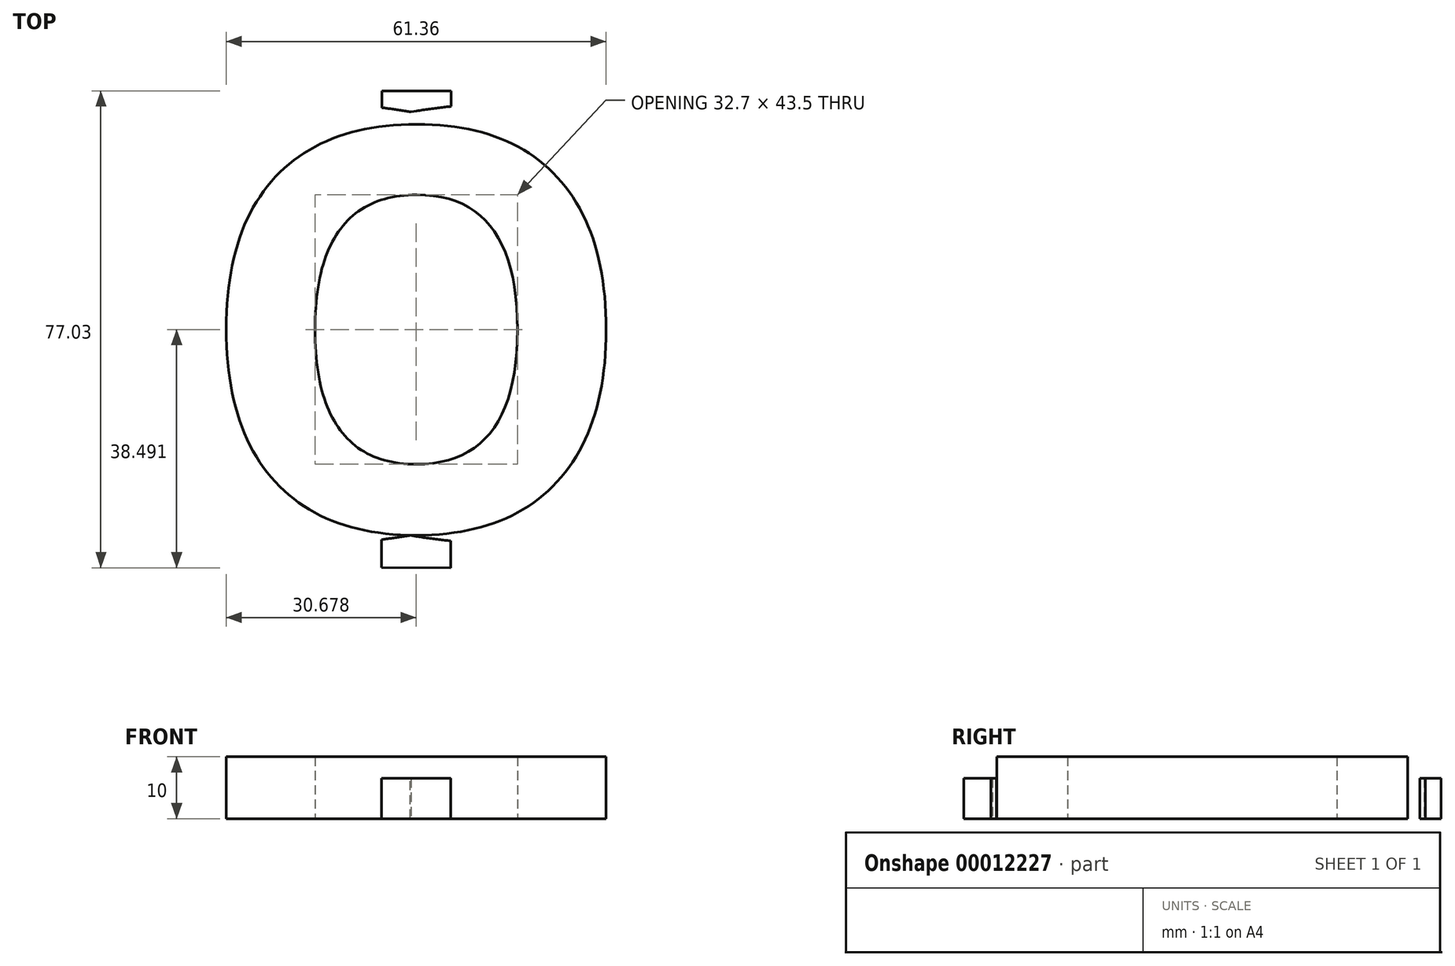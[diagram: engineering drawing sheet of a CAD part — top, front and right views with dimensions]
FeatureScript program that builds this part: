
annotation { "Feature Type Name" : "Feature", "Feature Type Description" : "" }
export const myFeature = defineFeature(function(context is Context, id is Id, definition is map)
    precondition{}
    {
        {
            var Q0;
            Q0=qCreatedBy(makeId("Top.planeOp"),FACE);
            var sketch = newSketch(context, id + "F0", { "sketchPlane" : qUnion([Q0])});
            skText(sketch, "E0", { "text": "O\n", "fontName": "OpenSans-Bold.ttf"});
            const initialGuessF0  = {"E0": [-0.0666, 0, 1, 0, 0.065]};
            skSetInitialGuess(sketch, initialGuessF0);
            skSolve(sketch);
        }
        {
            var Q0;
            Q0=makeQuery(id+"F0.imprint","IMPRINT",FACE,{"disambiguationData":[TD([[makeQuery(id+"F0.imprint","IMPRINT",EDGE,{"derivedFrom":sQuery(id+"F0.wireOp",EDGE,"E0.sketch_text.stroke-0")}),-1.0]])]});
            extrude(context, id + "F1", {"entities" : qUnion([Q0]), "depth" : 10 * mm});
        }
        {
            var Q0;
            Q0=qCreatedBy(makeId("Top.planeOp"),FACE);
            var sketch = newSketch(context, id + "F2", { "sketchPlane" : qUnion([Q0])});
            skFitSpline(sketch, "E1.0.0", {"points": [v(-8.18, 7.95) * mm, v(0, 16.8) * mm, v(0, 33.31) * mm]});
            skFitSpline(sketch, "E1.0.1", {"points": [v(0, 33.31) * mm, v(0, 49.84) * mm, v(-8.11, 58.66) * mm]});
            skFitSpline(sketch, "E1.0.2", {"points": [v(-8.11, 58.66) * mm, v(-16.23, 67.48) * mm, v(-31.54, 67.48) * mm]});
            skFitSpline(sketch, "E1.0.3", {"points": [v(-31.54, 67.48) * mm, v(-46.85, 67.48) * mm, v(-55.05, 58.73) * mm]});
            skFitSpline(sketch, "E1.0.4", {"points": [v(-55.05, 58.73) * mm, v(-63.25, 49.99) * mm, v(-63.25, 33.4) * mm]});
            skFitSpline(sketch, "E1.0.5", {"points": [v(-63.25, 33.4) * mm, v(-63.25, 16.8) * mm, v(-55.07, 7.95) * mm]});
            skFitSpline(sketch, "E1.0.6", {"points": [v(-55.07, 7.95) * mm, v(-46.9, -0.92) * mm, v(-31.62, -0.92) * mm]});
            skFitSpline(sketch, "E1.0.7", {"points": [v(-31.62, -0.92) * mm, v(-16.36, -0.92) * mm, v(-8.18, 7.95) * mm]});
            skLineSegment(sketch, "E2", {"start": v(-61.36, 32.4) * mm, "end": v(-61.36, 65.47) * mm, "construction": true});
            skLineSegment(sketch, "E3", {"start": v(-61.36, 65.47) * mm, "end": v(-30.6, 65.47) * mm, "construction": true});
            skLineSegment(sketch, "E4", {"start": v(-30.6, 65.47) * mm, "end": v(0, 65.47) * mm, "construction": true});
            skLineSegment(sketch, "E5", {"start": v(0, 65.47) * mm, "end": v(0, 32.32) * mm, "construction": true});
            skLineSegment(sketch, "E6", {"start": v(0, 0) * mm, "end": v(0, -0.89) * mm, "construction": true});
            skLineSegment(sketch, "E7", {"start": v(0, -0.89) * mm, "end": v(-30.68, -0.89) * mm, "construction": true});
            skLineSegment(sketch, "E8", {"start": v(-30.68, -0.89) * mm, "end": v(-61.36, -0.89) * mm, "construction": true});
            skLineSegment(sketch, "E9", {"start": v(-61.36, -0.89) * mm, "end": v(-61.36, 32.4) * mm, "construction": true});
            skLineSegment(sketch, "E10", {"start": v(-61.36, 0) * mm, "end": v(0, 0) * mm, "construction": true});
            skLineSegment(sketch, "E11", {"start": v(-61.36, 64.47) * mm, "end": v(0, 64.47) * mm, "construction": true});
            skLineSegment(sketch, "E12.bottom", {"start": v(-30.6, 64.47) * mm, "end": v(-36.2, 64.47) * mm});
            skLineSegment(sketch, "E12.top", {"start": v(-30.6, 70.87) * mm, "end": v(-36.2, 70.87) * mm});
            skLineSegment(sketch, "E12.left", {"start": v(-30.6, 64.47) * mm, "end": v(-30.6, 70.87) * mm});
            skLineSegment(sketch, "E12.right", {"start": v(-36.2, 64.47) * mm, "end": v(-36.2, 70.87) * mm});
            skLineSegment(sketch, "E13.bottom", {"start": v(-30.6, 64.47) * mm, "end": v(-25, 64.47) * mm});
            skLineSegment(sketch, "E13.top", {"start": v(-30.6, 70.87) * mm, "end": v(-25, 70.87) * mm});
            skLineSegment(sketch, "E13.right", {"start": v(-25, 64.47) * mm, "end": v(-25, 70.87) * mm});
            skLineSegment(sketch, "E14", {"start": v(-61.36, 32.4) * mm, "end": v(0, 32.32) * mm, "construction": true});
            skLineSegment(sketch, "E15", {"start": v(-61.36, 32.4) * mm, "end": v(0, 32.32) * mm});
            skLineSegment(sketch, "E16.0.MirrorCS", {"start": v(-30.7, -6.15) * mm, "end": v(-25.1, -6.16) * mm});
            skLineSegment(sketch, "E16.1.MirrorCS", {"start": v(-30.7, -6.15) * mm, "end": v(-36.3, -6.13) * mm});
            skLineSegment(sketch, "E16.2.MirrorCS", {"start": v(-25.09, 0.24) * mm, "end": v(-25.1, -6.16) * mm});
            skLineSegment(sketch, "E16.3.MirrorCS", {"start": v(-30.68, 0.25) * mm, "end": v(-25.09, 0.24) * mm});
            skLineSegment(sketch, "E16.4.MirrorCS", {"start": v(-30.68, 0.25) * mm, "end": v(-30.7, -6.15) * mm});
            skLineSegment(sketch, "E16.5.MirrorCS", {"start": v(-30.68, 0.25) * mm, "end": v(-36.28, 0.27) * mm});
            skLineSegment(sketch, "E16.6.MirrorCS", {"start": v(-36.28, 0.27) * mm, "end": v(-36.3, -6.13) * mm});
            skLineSegment(sketch, "E16.7.MirrorCS", {"start": v(-30.68, 0.25) * mm, "end": v(-30.7, -6.15) * mm});
            skSolve(sketch);
        }
        {
            var Q0;
            {var subQ1=sQuery(id+"F2.wireOp",EDGE,"E12.top");Q0=makeQuery(id+"F2.imprint","IMPRINT",FACE,{"disambiguationData":[TD([[makeQuery(id+"F2.imprint","IMPRINT",EDGE,{"derivedFrom":subQ1}),1.0]])]});}
            var Q1;
            {var subQ3=sQuery(id+"F2.wireOp",EDGE,"E13.top");Q1=makeQuery(id+"F2.imprint","IMPRINT",FACE,{"disambiguationData":[TD([[makeQuery(id+"F2.imprint","IMPRINT",EDGE,{"derivedFrom":subQ3}),-1.0]])]});}
            extrude(context, id + "F3", {"entities" : qUnion([Q0, Q1]), "operationType" : NewBodyOperationType.ADD, "depth" : 6.5 * mm});
        }
        {
            var Q0;
            {var subQ3=sQuery(id+"F2.wireOp",EDGE,"E16.1.MirrorCS");Q0=makeQuery(id+"F2.imprint","IMPRINT",FACE,{"disambiguationData":[TD([[makeQuery(id+"F2.imprint","IMPRINT",EDGE,{"derivedFrom":subQ3}),-1.0]])]});}
            var Q1;
            {var subQ1=sQuery(id+"F2.wireOp",EDGE,"E16.0.MirrorCS");Q1=makeQuery(id+"F2.imprint","IMPRINT",FACE,{"disambiguationData":[TD([[makeQuery(id+"F2.imprint","IMPRINT",EDGE,{"derivedFrom":subQ1}),1.0]])]});}
            extrude(context, id + "F4", {"entities" : qUnion([Q0, Q1]), "operationType" : NewBodyOperationType.ADD, "depth" : 6.5 * mm});
        }
    });
